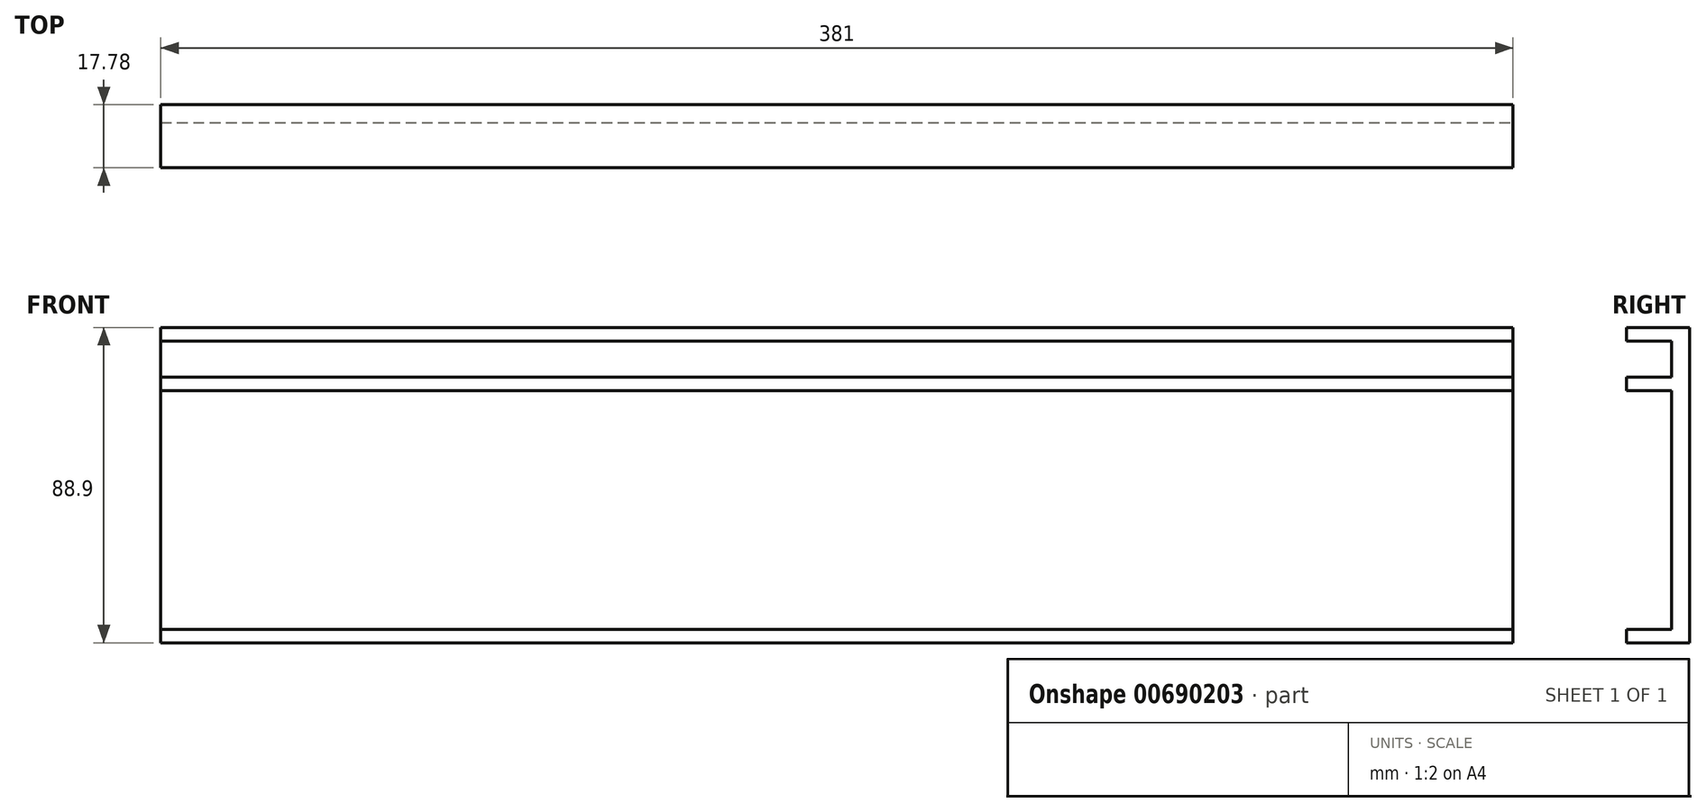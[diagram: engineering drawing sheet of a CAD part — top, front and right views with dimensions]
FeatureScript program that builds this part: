
annotation { "Feature Type Name" : "Feature", "Feature Type Description" : "" }
export const myFeature = defineFeature(function(context is Context, id is Id, definition is map)
    precondition{}
    {
        {
            var Q0;
            Q0=qCreatedBy(makeId("Front.planeOp"),FACE);
            var sketch = newSketch(context, id + "F0", { "sketchPlane" : qUnion([Q0])});
            skLineSegment(sketch, "E0.bottom", {"start": v(-190.5, -44.45) * mm, "end": v(190.5, -44.45) * mm});
            skLineSegment(sketch, "E0.top", {"start": v(-190.5, 44.45) * mm, "end": v(190.5, 44.45) * mm});
            skLineSegment(sketch, "E0.left", {"start": v(-190.5, -44.45) * mm, "end": v(-190.5, 44.45) * mm});
            skLineSegment(sketch, "E0.right", {"start": v(190.5, -44.45) * mm, "end": v(190.5, 44.45) * mm});
            skPoint(sketch, "E0.middle", {"position": v(0, 0) * mm});
            skSolve(sketch);
        }
        {
            var Q0;
            Q0=makeQuery(id+"F0.imprint","IMPRINT",FACE,{"disambiguationData":[TD([[makeQuery(id+"F0.imprint","IMPRINT",EDGE,{"derivedFrom":sQuery(id+"F0.wireOp",EDGE,"E0.bottom")}),1.0]])]});
            extrude(context, id + "F1", {"entities" : qUnion([Q0]), "depth" : 5.08 * mm, "offsetDistance" : 25.4 * mm});
        }
        {
            var Q0;
            Q0=makeQuery(id+"F1.opExtrude","CAP_FACE",FACE,{"disambiguationData":[OSD([sQuery(id+"F0.wireOp",EDGE,"E0.bottom"),sQuery(id+"F0.wireOp",EDGE,"E0.top"),sQuery(id+"F0.wireOp",EDGE,"E0.left"),sQuery(id+"F0.wireOp",EDGE,"E0.right")])],"isStart":false});
            var sketch = newSketch(context, id + "F2", { "sketchPlane" : qUnion([Q0])});
            skLineSegment(sketch, "E1", {"start": v(-190.5, 40.64) * mm, "end": v(190.5, 40.64) * mm});
            skLineSegment(sketch, "E2", {"start": v(-190.5, 40.64) * mm, "end": v(-190.5, 44.45) * mm});
            skLineSegment(sketch, "E3", {"start": v(-190.5, 44.45) * mm, "end": v(190.5, 44.45) * mm});
            skLineSegment(sketch, "E4", {"start": v(190.5, 44.45) * mm, "end": v(190.5, 40.64) * mm});
            skLineSegment(sketch, "E5", {"start": v(-190.5, -44.45) * mm, "end": v(190.5, -44.45) * mm});
            skLineSegment(sketch, "E6", {"start": v(190.5, -44.45) * mm, "end": v(190.5, -40.64) * mm});
            skLineSegment(sketch, "E7", {"start": v(190.5, -40.64) * mm, "end": v(-190.5, -40.64) * mm});
            skLineSegment(sketch, "E8", {"start": v(-190.5, -40.64) * mm, "end": v(-190.5, -44.45) * mm});
            skSolve(sketch);
        }
        {
            var Q0;
            Q0 = qSketchRegion(id + "F2", true);
            extrude(context, id + "F3", {"entities" : qUnion([Q0]), "operationType" : NewBodyOperationType.ADD, "depth" : 12.7 * mm, "offsetDistance" : 25.4 * mm});
        }
        {
            var Q0;
            Q0=makeQuery(id+"F1.opExtrude","CAP_FACE",FACE,{"disambiguationData":[OSD([sQuery(id+"F0.wireOp",EDGE,"E0.bottom"),sQuery(id+"F0.wireOp",EDGE,"E0.top"),sQuery(id+"F0.wireOp",EDGE,"E0.left"),sQuery(id+"F0.wireOp",EDGE,"E0.right")])],"isStart":false});
            var sketch = newSketch(context, id + "F4", { "sketchPlane" : qUnion([Q0])});
            skLineSegment(sketch, "E9", {"start": v(-190.5, 26.67) * mm, "end": v(190.5, 26.67) * mm});
            skLineSegment(sketch, "E10", {"start": v(-190.5, 30.48) * mm, "end": v(190.5, 30.48) * mm});
            skLineSegment(sketch, "E11", {"start": v(190.5, 30.48) * mm, "end": v(190.5, 26.67) * mm});
            skLineSegment(sketch, "E12", {"start": v(-190.5, 30.48) * mm, "end": v(-190.5, 26.67) * mm});
            skSolve(sketch);
        }
        {
            var Q0;
            Q0=makeQuery(id+"F4.imprint","IMPRINT",FACE,{"disambiguationData":[TD([[makeQuery(id+"F4.imprint","IMPRINT",EDGE,{"derivedFrom":sQuery(id+"F4.wireOp",EDGE,"E9")}),1.0]])]});
            extrude(context, id + "F5", {"entities" : qUnion([Q0]), "operationType" : NewBodyOperationType.ADD, "depth" : 12.7 * mm, "offsetDistance" : 25.4 * mm});
        }
    });
